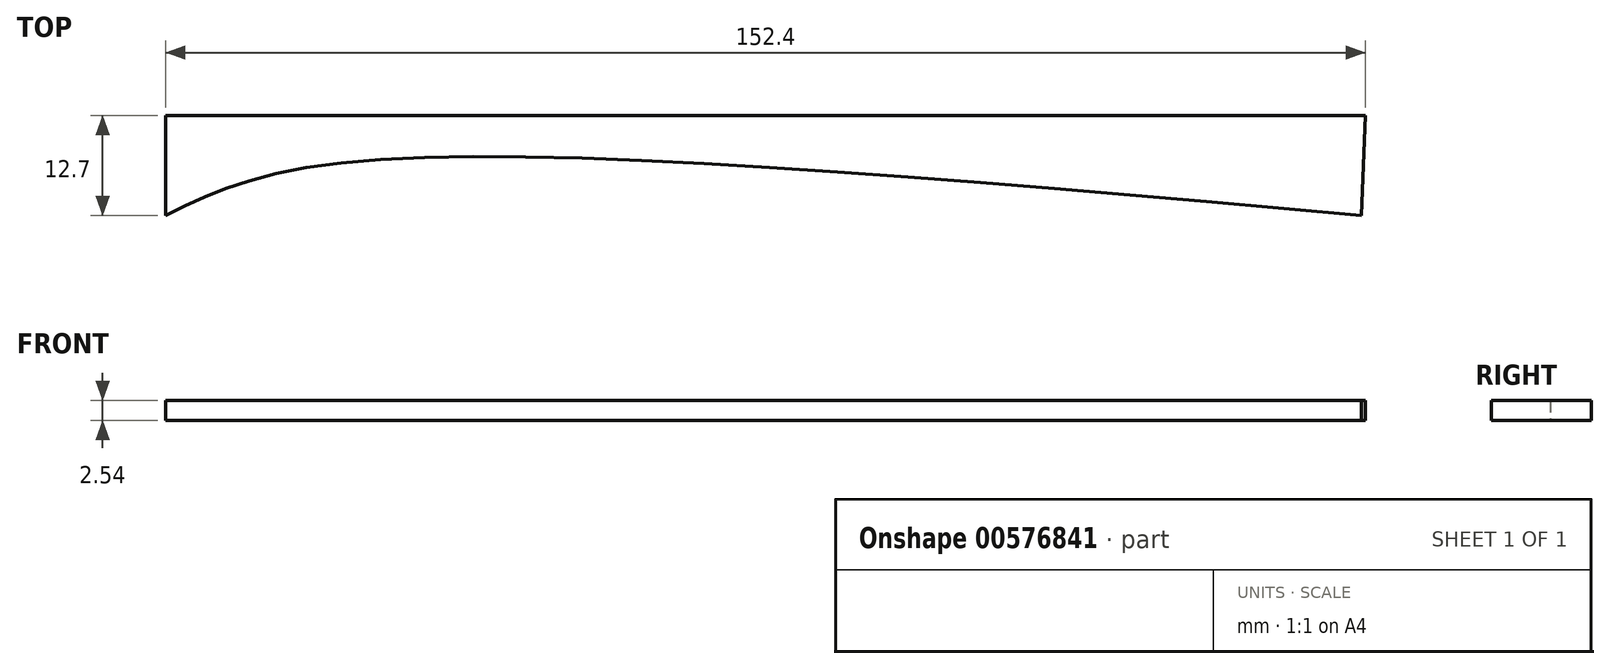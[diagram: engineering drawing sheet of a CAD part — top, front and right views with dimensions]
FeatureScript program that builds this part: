
annotation { "Feature Type Name" : "Feature", "Feature Type Description" : "" }
export const myFeature = defineFeature(function(context is Context, id is Id, definition is map)
    precondition{}
    {
        {
            var Q0;
            Q0=qCreatedBy(makeId("Top.planeOp"),FACE);
            var sketch = newSketch(context, id + "F0", { "sketchPlane" : qUnion([Q0])});
            skLineSegment(sketch, "E0.bottom", {"start": v(0, 0) * mm, "end": v(152.4, 0) * mm});
            skLineSegment(sketch, "E0.top", {"start": v(0, 12.7) * mm, "end": v(152.4, 12.7) * mm});
            skLineSegment(sketch, "E0.left", {"start": v(0, 0) * mm, "end": v(0, 12.7) * mm});
            skLineSegment(sketch, "E0.right", {"start": v(152.4, 0) * mm, "end": v(152.4, 12.7) * mm});
            skSolve(sketch);
        }
        {
            var Q0;
            Q0=makeQuery(id+"F0.imprint","IMPRINT",FACE,{"disambiguationData":[TD([[makeQuery(id+"F0.imprint","IMPRINT",EDGE,{"derivedFrom":sQuery(id+"F0.wireOp",EDGE,"E0.bottom")}),1.0]])]});
            var sketch = newSketch(context, id + "F1", { "sketchPlane" : qUnion([Q0])});
            skFitSpline(sketch, "E1", {"points": [v(0, 0) * mm, v(20.55, 6.45) * mm, v(151.92, 0) * mm], "startDerivative": vector(55.21, 27.04) * mm, "endDerivative": vector(228.14, -20.3) * mm});
            skLineSegment(sketch, "E2", {"start": v(0, 0) * mm, "end": v(0, 12.7) * mm});
            skLineSegment(sketch, "E3", {"start": v(0, 12.7) * mm, "end": v(152.4, 12.7) * mm});
            skLineSegment(sketch, "E4", {"start": v(152.4, 12.7) * mm, "end": v(151.92, 0) * mm});
            skSolve(sketch);
        }
        {
            var Q0;
            Q0=makeQuery(id+"F1.imprint","IMPRINT",FACE,{"disambiguationData":[TD([[makeQuery(id+"F1.imprint","IMPRINT",EDGE,{"derivedFrom":sQuery(id+"F1.wireOp",EDGE,"E1")}),1.0]])]});
            extrude(context, id + "F2", {"entities" : qUnion([Q0]), "depth" : 2.54 * mm, "offsetDistance" : 25.4 * mm});
        }
    });
